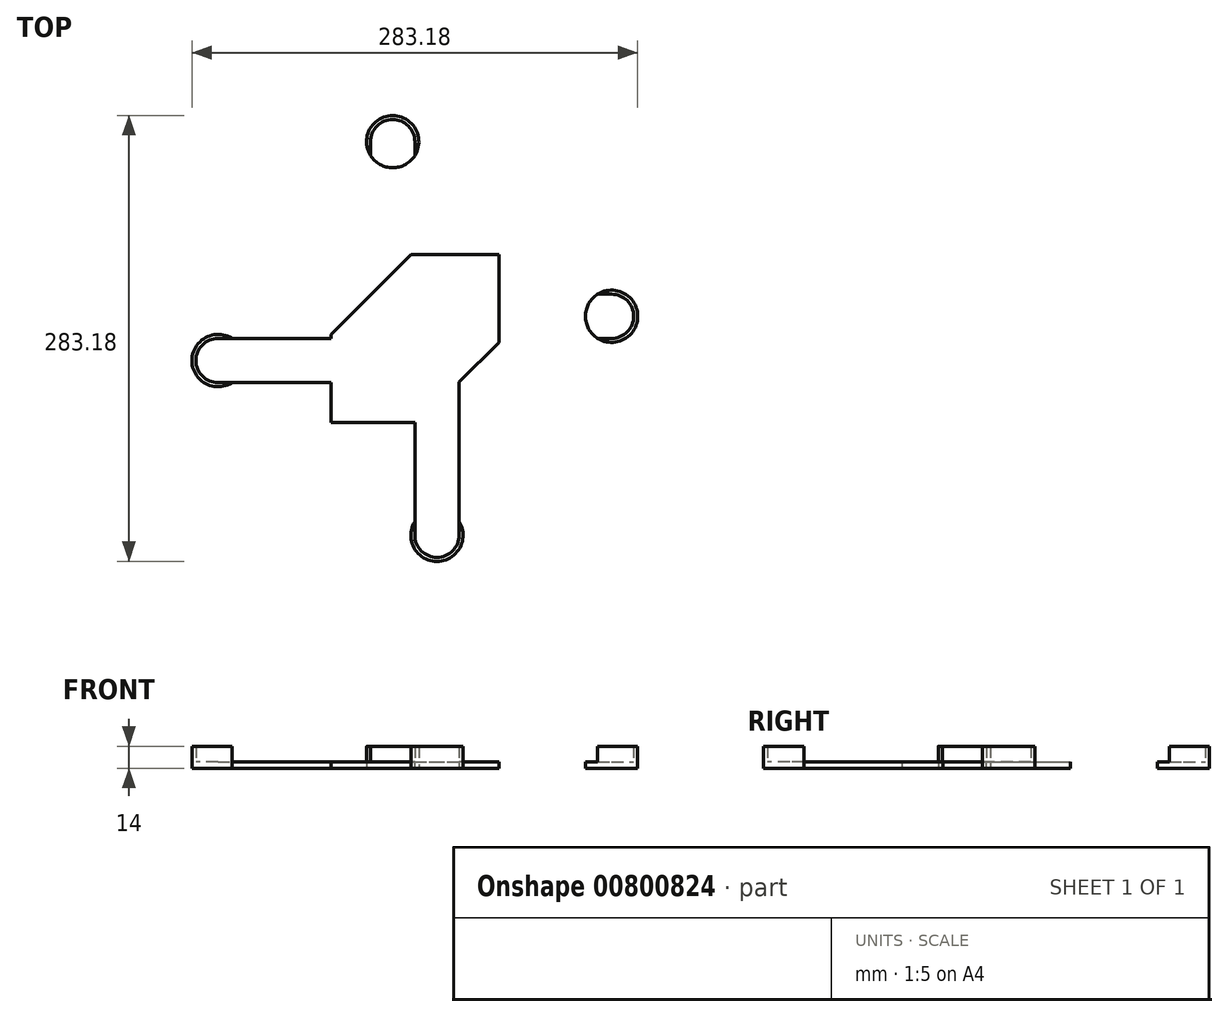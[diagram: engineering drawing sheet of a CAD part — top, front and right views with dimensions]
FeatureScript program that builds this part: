
annotation { "Feature Type Name" : "Feature", "Feature Type Description" : "" }
export const myFeature = defineFeature(function(context is Context, id is Id, definition is map)
    precondition{}
    {
        {
            var Q0;
            Q0=qCreatedBy(makeId("Top.planeOp"),FACE);
            var sketch = newSketch(context, id + "F0", { "sketchPlane" : qUnion([Q0])});
            skLineSegment(sketch, "E0.bottom", {"start": v(0, 0) * mm, "end": v(-28.1, 0) * mm});
            skLineSegment(sketch, "E0.top", {"start": v(0, 125) * mm, "end": v(-28.1, 125) * mm});
            skLineSegment(sketch, "E0.left", {"start": v(0, 0) * mm, "end": v(0, 125) * mm});
            skLineSegment(sketch, "E0.right", {"start": v(-28.1, 0) * mm, "end": v(-28.1, 125) * mm});
            skCircle(sketch, "E1", {"center": v(-14.05, 125) * mm, "radius": 14.05 * mm});
            skCircle(sketch, "E2.0", {"center": v(-14.05, 125) * mm, "radius": 16.59 * mm});
            skCircle(sketch, "E3.1.0", {"center": v(-125, -14.05) * mm, "radius": 16.59 * mm});
            skCircle(sketch, "E3.1.1", {"center": v(-125, -14.05) * mm, "radius": 14.05 * mm});
            skLineSegment(sketch, "E3.1.2", {"start": v(-125, 0) * mm, "end": v(-125, -28.1) * mm});
            skLineSegment(sketch, "E3.1.3", {"start": v(0, 0) * mm, "end": v(-125, 0) * mm});
            skLineSegment(sketch, "E3.1.4", {"start": v(0, -28.1) * mm, "end": v(-125, -28.1) * mm});
            skLineSegment(sketch, "E3.1.5", {"start": v(0, 0) * mm, "end": v(0, -28.1) * mm});
            skCircle(sketch, "E3.2.0", {"center": v(14.05, -125) * mm, "radius": 16.59 * mm});
            skCircle(sketch, "E3.2.1", {"center": v(14.05, -125) * mm, "radius": 14.05 * mm});
            skLineSegment(sketch, "E3.2.2", {"start": v(0, -125) * mm, "end": v(28.1, -125) * mm});
            skLineSegment(sketch, "E3.2.3", {"start": v(0, 0) * mm, "end": v(0, -125) * mm});
            skLineSegment(sketch, "E3.2.4", {"start": v(28.1, 0) * mm, "end": v(28.1, -125) * mm});
            skLineSegment(sketch, "E3.2.5", {"start": v(0, 0) * mm, "end": v(28.1, 0) * mm});
            skCircle(sketch, "E3.3.0", {"center": v(125, 14.05) * mm, "radius": 16.59 * mm});
            skCircle(sketch, "E3.3.1", {"center": v(125, 14.05) * mm, "radius": 14.05 * mm});
            skLineSegment(sketch, "E3.3.2", {"start": v(125, 0) * mm, "end": v(125, 28.1) * mm});
            skLineSegment(sketch, "E3.3.3", {"start": v(0, 0) * mm, "end": v(125, 0) * mm});
            skLineSegment(sketch, "E3.3.4", {"start": v(0, 28.1) * mm, "end": v(125, 28.1) * mm});
            skLineSegment(sketch, "E3.3.5", {"start": v(0, 0) * mm, "end": v(0, 28.1) * mm});
            skPoint(sketch, "E3.center", {"position": v(0, 0) * mm});
            skSolve(sketch);
        }
        {
            var Q0;
            {var subQ0=sQuery(id+"F0.wireOp",EDGE,"E0.top");Q0=makeQuery(id+"F0.imprint","IMPRINT",FACE,{"disambiguationData":[TD([[makeQuery(id+"F0.imprint","IMPRINT",EDGE,{"derivedFrom":subQ0}),-1.0]])]});}
            var Q1;
            {var subQ0=sQuery(id+"F0.wireOp",EDGE,"E0.top");Q1=makeQuery(id+"F0.imprint","IMPRINT",FACE,{"disambiguationData":[TD([[makeQuery(id+"F0.imprint","IMPRINT",EDGE,{"derivedFrom":subQ0}),1.0]])]});}
            var Q2;
            {var subQ1=sQuery(id+"F0.wireOp",EDGE,"E0.left");var subQ4=sQuery(id+"F0.wireOp",EDGE,"E2.0");var subQ5=makeQuery(id+"F0.imprint","INTERSECT",VERTEX,{"derivedFrom":[subQ1,subQ4]});Q2=makeQuery(id+"F0.imprint","IMPRINT",FACE,{"disambiguationData":[TD([[makeQuery(id+"F0.imprint","IMPRINT",EDGE,{"disambiguationData":[TD([[subQ5,1.0]])],"derivedFrom":subQ4}),1.0]])]});}
            var Q3;
            {var subQ3=sQuery(id+"F0.wireOp",EDGE,"E3.3.5");Q3=makeQuery(id+"F0.imprint","IMPRINT",FACE,{"disambiguationData":[TD([[makeQuery(id+"F0.imprint","IMPRINT",EDGE,{"derivedFrom":subQ3}),1.0]])]});}
            var Q4;
            {var subQ0=sQuery(id+"F0.wireOp",EDGE,"E3.3.5");Q4=makeQuery(id+"F0.imprint","IMPRINT",FACE,{"disambiguationData":[TD([[makeQuery(id+"F0.imprint","IMPRINT",EDGE,{"derivedFrom":subQ0}),-1.0]])]});}
            var Q5;
            {var subQ0=sQuery(id+"F0.wireOp",EDGE,"E3.3.2");Q5=makeQuery(id+"F0.imprint","IMPRINT",FACE,{"disambiguationData":[TD([[makeQuery(id+"F0.imprint","IMPRINT",EDGE,{"derivedFrom":subQ0}),-1.0]])]});}
            var Q6;
            {var subQ0=sQuery(id+"F0.wireOp",EDGE,"E3.3.2");Q6=makeQuery(id+"F0.imprint","IMPRINT",FACE,{"disambiguationData":[TD([[makeQuery(id+"F0.imprint","IMPRINT",EDGE,{"derivedFrom":subQ0}),1.0]])]});}
            var Q7;
            {var subQ3=sQuery(id+"F0.wireOp",EDGE,"E3.2.0");var subQ5=sQuery(id+"F0.wireOp",EDGE,"E3.2.3");var subQ7=makeQuery(id+"F0.imprint","INTERSECT",VERTEX,{"derivedFrom":[subQ3,subQ5]});Q7=makeQuery(id+"F0.imprint","IMPRINT",FACE,{"disambiguationData":[TD([[makeQuery(id+"F0.imprint","IMPRINT",EDGE,{"disambiguationData":[TD([[subQ7,1.0]])],"derivedFrom":subQ3}),-1.0]])]});}
            var Q8;
            {var subQ0=sQuery(id+"F0.wireOp",EDGE,"E3.2.2");Q8=makeQuery(id+"F0.imprint","IMPRINT",FACE,{"disambiguationData":[TD([[makeQuery(id+"F0.imprint","IMPRINT",EDGE,{"derivedFrom":subQ0}),-1.0]])]});}
            var Q9;
            {var subQ0=sQuery(id+"F0.wireOp",EDGE,"E3.2.2");Q9=makeQuery(id+"F0.imprint","IMPRINT",FACE,{"disambiguationData":[TD([[makeQuery(id+"F0.imprint","IMPRINT",EDGE,{"derivedFrom":subQ0}),1.0]])]});}
            var Q10;
            {var subQ0=sQuery(id+"F0.wireOp",EDGE,"E3.2.3");var subQ1=sQuery(id+"F0.wireOp",EDGE,"E3.2.0");var subQ2=makeQuery(id+"F0.imprint","INTERSECT",VERTEX,{"derivedFrom":[subQ1,subQ0]});Q10=makeQuery(id+"F0.imprint","IMPRINT",FACE,{"disambiguationData":[TD([[makeQuery(id+"F0.imprint","IMPRINT",EDGE,{"disambiguationData":[TD([[subQ2,1.0]])],"derivedFrom":subQ1}),1.0]])]});}
            var Q11;
            {var subQ0=sQuery(id+"F0.wireOp",EDGE,"E3.1.2");Q11=makeQuery(id+"F0.imprint","IMPRINT",FACE,{"disambiguationData":[TD([[makeQuery(id+"F0.imprint","IMPRINT",EDGE,{"derivedFrom":subQ0}),-1.0]])]});}
            var Q12;
            {var subQ0=sQuery(id+"F0.wireOp",EDGE,"E3.1.2");Q12=makeQuery(id+"F0.imprint","IMPRINT",FACE,{"disambiguationData":[TD([[makeQuery(id+"F0.imprint","IMPRINT",EDGE,{"derivedFrom":subQ0}),1.0]])]});}
            var Q13;
            {var subQ0=sQuery(id+"F0.wireOp",EDGE,"E3.1.3");var subQ1=sQuery(id+"F0.wireOp",EDGE,"E3.1.0");var subQ2=makeQuery(id+"F0.imprint","INTERSECT",VERTEX,{"derivedFrom":[subQ1,subQ0]});Q13=makeQuery(id+"F0.imprint","IMPRINT",FACE,{"disambiguationData":[TD([[makeQuery(id+"F0.imprint","IMPRINT",EDGE,{"disambiguationData":[TD([[subQ2,1.0]])],"derivedFrom":subQ1}),1.0]])]});}
            var Q14;
            {var subQ3=sQuery(id+"F0.wireOp",EDGE,"E3.1.0");var subQ5=sQuery(id+"F0.wireOp",EDGE,"E3.1.3");var subQ7=makeQuery(id+"F0.imprint","INTERSECT",VERTEX,{"derivedFrom":[subQ3,subQ5]});Q14=makeQuery(id+"F0.imprint","IMPRINT",FACE,{"disambiguationData":[TD([[makeQuery(id+"F0.imprint","IMPRINT",EDGE,{"disambiguationData":[TD([[subQ7,1.0]])],"derivedFrom":subQ3}),-1.0]])]});}
            var Q15;
            {var subQ0=sQuery(id+"F0.wireOp",EDGE,"E3.3.3");var subQ1=sQuery(id+"F0.wireOp",EDGE,"E3.3.0");var subQ2=makeQuery(id+"F0.imprint","INTERSECT",VERTEX,{"derivedFrom":[subQ1,subQ0]});Q15=makeQuery(id+"F0.imprint","IMPRINT",FACE,{"disambiguationData":[TD([[makeQuery(id+"F0.imprint","IMPRINT",EDGE,{"disambiguationData":[TD([[subQ2,1.0]])],"derivedFrom":subQ1}),1.0]])]});}
            extrude(context, id + "F1", {"entities" : qUnion([Q0, Q1, Q2, Q3, Q4, Q5, Q6, Q7, Q8, Q9, Q10, Q11, Q12, Q13, Q14, Q15]), "depth" : 4 * mm, "offsetDistance" : 25.4 * mm});
        }
        {
            var Q0;
            {var subQ1=sQuery(id+"F0.wireOp",EDGE,"E0.left");var subQ4=sQuery(id+"F0.wireOp",EDGE,"E2.0");var subQ5=makeQuery(id+"F0.imprint","INTERSECT",VERTEX,{"derivedFrom":[subQ1,subQ4]});Q0=makeQuery(id+"F0.imprint","IMPRINT",FACE,{"disambiguationData":[TD([[makeQuery(id+"F0.imprint","IMPRINT",EDGE,{"disambiguationData":[TD([[subQ5,-1.0]])],"derivedFrom":subQ4}),1.0]])]});}
            var Q1;
            {var subQ0=sQuery(id+"F0.wireOp",EDGE,"E3.3.3");var subQ1=sQuery(id+"F0.wireOp",EDGE,"E3.3.0");var subQ2=makeQuery(id+"F0.imprint","INTERSECT",VERTEX,{"derivedFrom":[subQ1,subQ0]});Q1=makeQuery(id+"F0.imprint","IMPRINT",FACE,{"disambiguationData":[TD([[makeQuery(id+"F0.imprint","IMPRINT",EDGE,{"disambiguationData":[TD([[subQ2,-1.0]])],"derivedFrom":subQ1}),1.0]])]});}
            var Q2;
            {var subQ0=sQuery(id+"F0.wireOp",EDGE,"E3.2.3");var subQ1=sQuery(id+"F0.wireOp",EDGE,"E3.2.0");var subQ2=makeQuery(id+"F0.imprint","INTERSECT",VERTEX,{"derivedFrom":[subQ1,subQ0]});Q2=makeQuery(id+"F0.imprint","IMPRINT",FACE,{"disambiguationData":[TD([[makeQuery(id+"F0.imprint","IMPRINT",EDGE,{"disambiguationData":[TD([[subQ2,-1.0]])],"derivedFrom":subQ1}),1.0]])]});}
            var Q3;
            {var subQ0=sQuery(id+"F0.wireOp",EDGE,"E3.1.3");var subQ1=sQuery(id+"F0.wireOp",EDGE,"E3.1.0");var subQ2=makeQuery(id+"F0.imprint","INTERSECT",VERTEX,{"derivedFrom":[subQ1,subQ0]});Q3=makeQuery(id+"F0.imprint","IMPRINT",FACE,{"disambiguationData":[TD([[makeQuery(id+"F0.imprint","IMPRINT",EDGE,{"disambiguationData":[TD([[subQ2,-1.0]])],"derivedFrom":subQ1}),1.0]])]});}
            extrude(context, id + "F2", {"entities" : qUnion([Q0, Q1, Q2, Q3]), "operationType" : NewBodyOperationType.ADD, "depth" : 4 * mm + 10 * mm, "offsetDistance" : 25.4 * mm});
        }
        {
            var Q0;
            Q0=makeQuery(id+"F1.opExtrude","CAP_FACE",FACE,{"disambiguationData":[OSD([sQuery(id+"F0.wireOp",EDGE,"E0.left"),sQuery(id+"F0.wireOp",EDGE,"E0.right"),sQuery(id+"F0.wireOp",EDGE,"E1"),sQuery(id+"F0.wireOp",EDGE,"E3.1.1"),sQuery(id+"F0.wireOp",EDGE,"E3.1.3"),sQuery(id+"F0.wireOp",EDGE,"E3.1.4"),sQuery(id+"F0.wireOp",EDGE,"E3.2.1"),sQuery(id+"F0.wireOp",EDGE,"E3.2.3"),sQuery(id+"F0.wireOp",EDGE,"E3.2.4"),sQuery(id+"F0.wireOp",EDGE,"E3.3.1"),sQuery(id+"F0.wireOp",EDGE,"E3.3.3"),sQuery(id+"F0.wireOp",EDGE,"E3.3.4")])],"isStart":false});
            var sketch = newSketch(context, id + "F3", { "sketchPlane" : qUnion([Q0])});
            skLineSegment(sketch, "E4.bottom", {"start": v(0, 0) * mm, "end": v(53.35, 0) * mm});
            skLineSegment(sketch, "E4.top", {"start": v(0, 53.35) * mm, "end": v(53.35, 53.35) * mm});
            skLineSegment(sketch, "E4.left", {"start": v(0, 0) * mm, "end": v(0, 53.35) * mm});
            skLineSegment(sketch, "E4.right", {"start": v(53.35, 0) * mm, "end": v(53.35, 53.35) * mm});
            skLineSegment(sketch, "E5.1.0", {"start": v(0, 53.35) * mm, "end": v(-53.35, 53.35) * mm});
            skLineSegment(sketch, "E5.1.1", {"start": v(-53.35, 0) * mm, "end": v(-53.35, 53.35) * mm});
            skLineSegment(sketch, "E5.1.2", {"start": v(0, 0) * mm, "end": v(-53.35, 0) * mm});
            skLineSegment(sketch, "E5.2.0", {"start": v(-53.35, 0) * mm, "end": v(-53.35, -53.35) * mm});
            skLineSegment(sketch, "E5.2.1", {"start": v(0, -53.35) * mm, "end": v(-53.35, -53.35) * mm});
            skLineSegment(sketch, "E5.2.2", {"start": v(0, 0) * mm, "end": v(0, -53.35) * mm});
            skLineSegment(sketch, "E5.2.3", {"start": v(0, 0) * mm, "end": v(-53.35, 0) * mm});
            skLineSegment(sketch, "E5.3.0", {"start": v(0, -53.35) * mm, "end": v(53.35, -53.35) * mm});
            skLineSegment(sketch, "E5.3.1", {"start": v(53.35, 0) * mm, "end": v(53.35, -53.35) * mm});
            skLineSegment(sketch, "E5.3.3", {"start": v(0, 0) * mm, "end": v(0, -53.35) * mm});
            skPoint(sketch, "E5.center", {"position": v(0, 0) * mm});
            skSolve(sketch);
        }
        {
            var Q0;
            {var subQ0=sQuery(id+"F3.wireOp",EDGE,"E4.top");Q0=makeQuery(id+"F3.imprint","IMPRINT",FACE,{"disambiguationData":[TD([[makeQuery(id+"F3.imprint","IMPRINT",EDGE,{"derivedFrom":subQ0}),-1.0]])]});}
            extrude(context, id + "F4", {"entities" : qUnion([Q0]), "operationType" : NewBodyOperationType.ADD, "oppositeDirection" : true, "depth" : 4 * mm, "offsetDistance" : 25.4 * mm});
        }
        {
            var Q0;
            {var subQ0=sQuery(id+"F3.wireOp",EDGE,"E5.3.1");Q0=makeQuery(id+"F3.imprint","IMPRINT",FACE,{"disambiguationData":[TD([[makeQuery(id+"F3.imprint","IMPRINT",EDGE,{"derivedFrom":subQ0}),-1.0]])]});}
            var Q1;
            {var subQ0=sQuery(id+"F3.wireOp",EDGE,"E5.2.1");Q1=makeQuery(id+"F3.imprint","IMPRINT",FACE,{"disambiguationData":[TD([[makeQuery(id+"F3.imprint","IMPRINT",EDGE,{"derivedFrom":subQ0}),-1.0]])]});}
            var Q2;
            {var subQ0=sQuery(id+"F3.wireOp",EDGE,"E5.1.1");Q2=makeQuery(id+"F3.imprint","IMPRINT",FACE,{"disambiguationData":[TD([[makeQuery(id+"F3.imprint","IMPRINT",EDGE,{"derivedFrom":subQ0}),-1.0]])]});}
            extrude(context, id + "F5", {"entities" : qUnion([Q0, Q1, Q2]), "operationType" : NewBodyOperationType.ADD, "oppositeDirection" : true, "depth" : 4 * mm, "offsetDistance" : 25.4 * mm});
        }
        {
            var Q0;
            Q0=makeQuery(id+"F5.opExtrude","SWEPT_EDGE",EDGE,{"disambiguationData":[OSD([sQuery(id+"F3.wireOp",EDGE,"E5.3.0"),sQuery(id+"F3.wireOp",EDGE,"E5.3.1")])]});
            var Q1;
            Q1=makeQuery(id+"F5.opExtrude","SWEPT_EDGE",EDGE,{"disambiguationData":[OSD([sQuery(id+"F3.wireOp",EDGE,"E5.1.0"),sQuery(id+"F3.wireOp",EDGE,"E5.1.1")])]});
            chamfer(context, id + "F6", {"entities" : qUnion([Q0, Q1]), "width" : 50.8 * mm, "tangentPropagation" : true});
        }
    });
